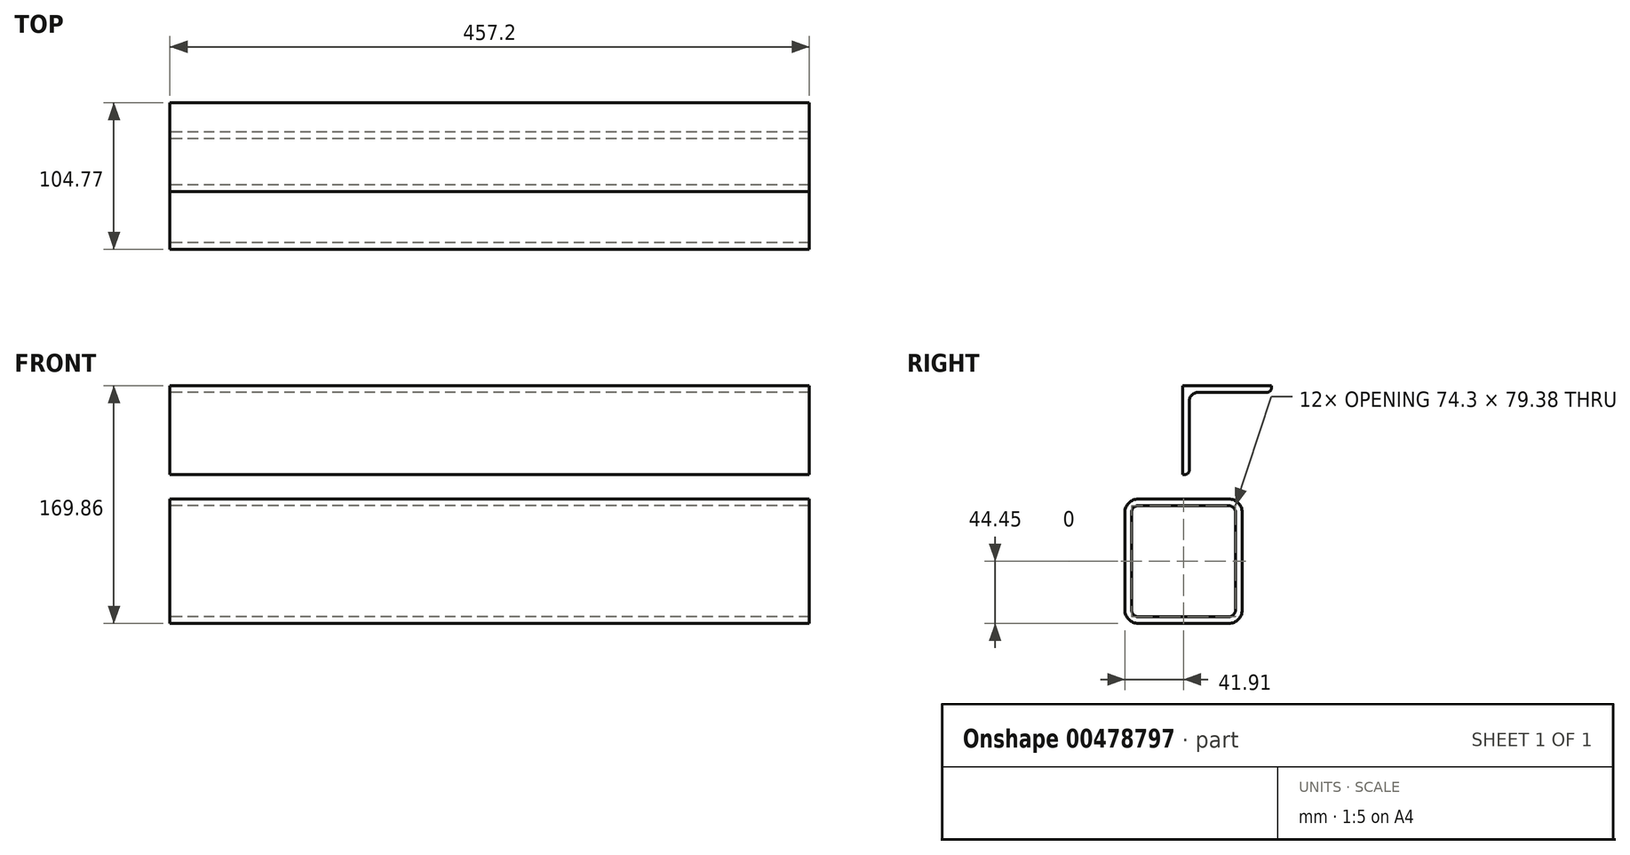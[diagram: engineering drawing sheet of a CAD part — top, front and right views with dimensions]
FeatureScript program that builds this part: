
annotation { "Feature Type Name" : "Feature", "Feature Type Description" : "" }
export const myFeature = defineFeature(function(context is Context, id is Id, definition is map)
    precondition{}
    {
        {
            var Q0;
            Q0=qCreatedBy(makeId("Right.planeOp"),FACE);
            var sketch = newSketch(context, id + "F0", { "sketchPlane" : qUnion([Q0])});
            skLineSegment(sketch, "E0.bottom", {"start": v(9.53, 0) * mm, "end": v(74.3, 0) * mm});
            skLineSegment(sketch, "E0.top", {"start": v(9.52, -88.9) * mm, "end": v(74.3, -88.9) * mm});
            skLineSegment(sketch, "E0.left", {"start": v(0, -9.52) * mm, "end": v(0, -79.37) * mm});
            skLineSegment(sketch, "E0.right", {"start": v(83.82, -9.52) * mm, "end": v(83.82, -79.37) * mm});
            skPoint(sketch, "E1.visualSharp", {"position": v(0, 0) * mm});
            skArc(sketch, "E1.filletArc", {"start": v(9.53, 0) * mm, "mid": v(2.79, -2.79) * mm, "end": v(0, -9.52) * mm});
            skPoint(sketch, "E2.visualSharp", {"position": v(83.82, 0) * mm});
            skArc(sketch, "E2.filletArc", {"start": v(83.82, -9.52) * mm, "mid": v(81.03, -2.79) * mm, "end": v(74.3, 0) * mm});
            skPoint(sketch, "E3.visualSharp", {"position": v(83.82, -88.9) * mm});
            skArc(sketch, "E3.filletArc", {"start": v(74.3, -88.9) * mm, "mid": v(81.03, -86.11) * mm, "end": v(83.82, -79.37) * mm});
            skPoint(sketch, "E4.visualSharp", {"position": v(0, -88.9) * mm});
            skArc(sketch, "E4.filletArc", {"start": v(0, -79.37) * mm, "mid": v(2.79, -86.11) * mm, "end": v(9.52, -88.9) * mm});
            skArc(sketch, "E5.0", {"start": v(9.53, -4.76) * mm, "mid": v(6.16, -6.16) * mm, "end": v(4.76, -9.52) * mm});
            skLineSegment(sketch, "E5.1", {"start": v(4.76, -9.52) * mm, "end": v(4.76, -79.38) * mm});
            skLineSegment(sketch, "E5.2", {"start": v(9.52, -4.76) * mm, "end": v(74.3, -4.76) * mm});
            skArc(sketch, "E5.3", {"start": v(4.76, -79.38) * mm, "mid": v(6.16, -82.74) * mm, "end": v(9.53, -84.14) * mm});
            skArc(sketch, "E5.4", {"start": v(79.06, -9.52) * mm, "mid": v(77.66, -6.16) * mm, "end": v(74.3, -4.76) * mm});
            skLineSegment(sketch, "E5.5", {"start": v(79.06, -9.52) * mm, "end": v(79.06, -79.38) * mm});
            skArc(sketch, "E5.6", {"start": v(74.3, -84.14) * mm, "mid": v(77.66, -82.74) * mm, "end": v(79.06, -79.38) * mm});
            skLineSegment(sketch, "E5.7", {"start": v(9.53, -84.14) * mm, "end": v(74.3, -84.14) * mm});
            skSolve(sketch);
        }
        {
            var Q0;
            Q0=makeQuery(id+"F0.imprint","IMPRINT",FACE,{"disambiguationData":[TD([[makeQuery(id+"F0.imprint","IMPRINT",EDGE,{"derivedFrom":sQuery(id+"F0.wireOp",EDGE,"E0.bottom")}),-1.0]])]});
            extrude(context, id + "F1", {"entities" : qUnion([Q0]), "endBound" : BoundingType.SYMMETRIC, "depth" : 457.2 * mm});
        }
        {
            var Q0;
            Q0=qCreatedBy(makeId("Right.planeOp"),FACE);
            var sketch = newSketch(context, id + "F2", { "sketchPlane" : qUnion([Q0])});
            skLineSegment(sketch, "E6", {"start": v(41.28, 17.46) * mm, "end": v(41.28, 80.96) * mm});
            skLineSegment(sketch, "E7", {"start": v(41.28, 80.96) * mm, "end": v(104.78, 80.96) * mm});
            skLineSegment(sketch, "E8", {"start": v(104.78, 80.96) * mm, "end": v(104.78, 79.38) * mm});
            skLineSegment(sketch, "E9", {"start": v(101.6, 76.2) * mm, "end": v(52.39, 76.2) * mm});
            skLineSegment(sketch, "E10", {"start": v(46.04, 69.85) * mm, "end": v(46.04, 20.64) * mm});
            skLineSegment(sketch, "E11", {"start": v(42.86, 17.46) * mm, "end": v(41.28, 17.46) * mm});
            skPoint(sketch, "E12.visualSharp", {"position": v(46.04, 76.2) * mm});
            skArc(sketch, "E12.filletArc", {"start": v(52.39, 76.2) * mm, "mid": v(47.9, 74.34) * mm, "end": v(46.04, 69.85) * mm});
            skPoint(sketch, "E13.visualSharp", {"position": v(104.78, 76.2) * mm});
            skArc(sketch, "E13.filletArc", {"start": v(101.6, 76.2) * mm, "mid": v(103.85, 77.13) * mm, "end": v(104.78, 79.38) * mm});
            skPoint(sketch, "E14.visualSharp", {"position": v(46.04, 17.46) * mm});
            skArc(sketch, "E14.filletArc", {"start": v(42.86, 17.46) * mm, "mid": v(45.1, 18.4) * mm, "end": v(46.04, 20.64) * mm});
            skSolve(sketch);
        }
        {
            var Q0;
            Q0=makeQuery(id+"F2.imprint","IMPRINT",FACE,{"disambiguationData":[TD([[makeQuery(id+"F2.imprint","IMPRINT",EDGE,{"derivedFrom":sQuery(id+"F2.wireOp",EDGE,"E6")}),-1.0]])]});
            extrude(context, id + "F3", {"entities" : qUnion([Q0]), "endBound" : BoundingType.SYMMETRIC, "depth" : 457.2 * mm});
        }
    });
